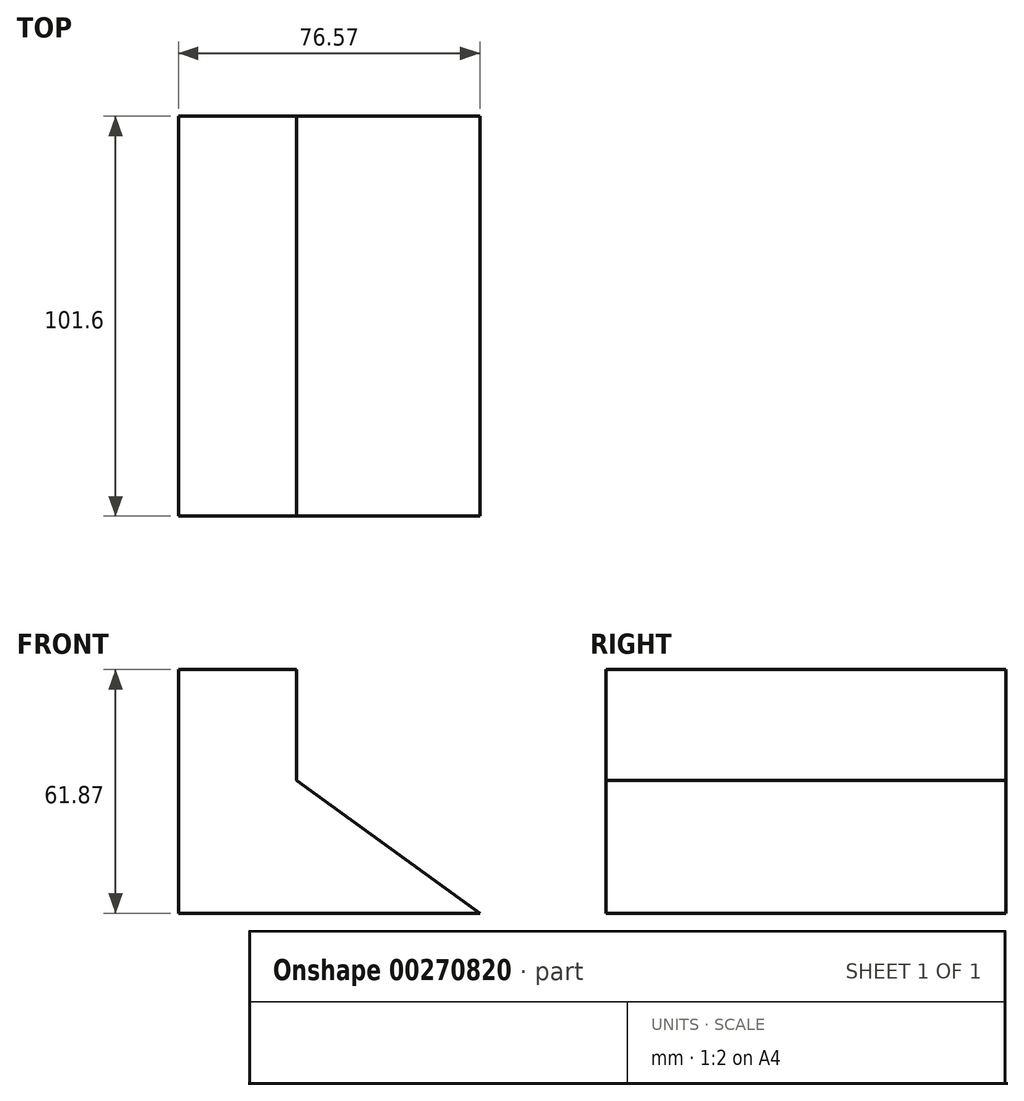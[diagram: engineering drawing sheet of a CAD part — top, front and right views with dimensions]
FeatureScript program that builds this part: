
annotation { "Feature Type Name" : "Feature", "Feature Type Description" : "" }
export const myFeature = defineFeature(function(context is Context, id is Id, definition is map)
    precondition{}
    {
        {
            var Q0;
            Q0=qCreatedBy(makeId("Front.planeOp"),FACE);
            var sketch = newSketch(context, id + "F0", { "sketchPlane" : qUnion([Q0])});
            skLineSegment(sketch, "E0", {"start": v(-76.57, 0) * mm, "end": v(-76.57, 61.87) * mm});
            skLineSegment(sketch, "E1", {"start": v(-76.57, 61.87) * mm, "end": v(-46.6, 61.87) * mm});
            skLineSegment(sketch, "E2", {"start": v(-76.57, 0) * mm, "end": v(0, 0) * mm});
            skLineSegment(sketch, "E3", {"start": v(-46.6, 61.87) * mm, "end": v(-46.6, 33.8) * mm});
            skLineSegment(sketch, "E4", {"start": v(-46.6, 33.8) * mm, "end": v(0, 0) * mm});
            skSolve(sketch);
        }
        {
            var Q0;
            Q0 = qSketchRegion(id + "F0", true);
            extrude(context, id + "F1", {"entities" : qUnion([Q0]), "depth" : 101.6 * mm});
        }
    });
